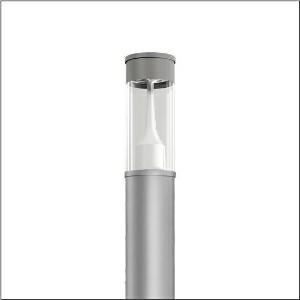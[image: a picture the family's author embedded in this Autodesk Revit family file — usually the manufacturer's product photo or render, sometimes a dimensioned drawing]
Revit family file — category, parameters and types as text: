
# Revit family: city-light_260_iq___pl1_2s_5xa5295of14h_8957
name_source: partatom
category: Lighting Fixtures
units: mm (PartAtom-declared; Revit-internal decimal feet)

## family parameters
Cut with Voids When Loaded = No
Host = Face
Light Source = No
Part Type = Normal
Room Calculation Point = No
Round Connector Dimension = Use Diameter
Shared = No

## types (1)
- --- (1 x LED, 2970 lm, 21.8 W, 2700K)
    Apparent Load = 22 VA
    CIE Flux Codes = 23 62 94 96 100
    Color Rendering = 70
    Color Temperature = 2700K
    Default Elevation = 1800 mm
    Description = City-Light 260 iQ, light pillar, Module 540 iQ-SR, primary light control with 3 zone facetted reflector, of plastic, silver coated, highly specular, structured, primary optical cover: cover, of PMMA, transparent, partly coated, light distribution: PL1.2s, primary light characteristic: symmetric, LED, High Power LED, rated luminous flux: 2.970lm, luminous efficacy: 136lm/W, light colour: 727, colour temperature: 2700K, control gear: iQ Street-Remote, control: pre-setting: logarithmic dimming characteristic, Street-Remote, Auto-Match, Temp-Guard, Lumen-Switch, Night-Set, Smart-Wire, Light-Fading, Desk-Remote (wireless, voltage-free reading and setting of iQ features in the workshop via application-optimized NFC function/RFID function), optimised constant luminous flux control (CLO 2.0), with terminal, 6-pole, max. 2.5mm², mains connection: 230..240V, AC, 50/60Hz, start of lifetime: 22W, end of service life: 23W, reduction: 11W, luminaire housing, cylindrical, of extruded aluminium section, coated, Siteco® metallic grey (DB 702S), length: 2.600mm, diameter: 200mm, Module 540 iQ-SR, traffic white (RAL 9016), equipment: standard, protection rating (complete): IP65, insulation class (complete): insulation class II (safety insulation), certification: CE, ENEC, VDE, packaging unit: 1 piece

Light Distribution: PL1.2s
    Height = 500 mm
    Lamp = 1 x LED
    Lamp Light Flux = 2970 lm
    Lamp Power = 21.8 W
    Lamp count = 1
    Length = 200 mm  [stored 0.656168 ft]
    Luminous efficacy = 136 lm/W
    Manufacturer = Siteco
    ModVariant = No
    Model = 5XA5295OF14H
    Mounting Place = Floor
    Mounting Type = Freestanding
    Number of Poles = 1
    OnlyDefault = Yes
    Power Factor = 1
    Product Name = City-Light 260 iQ | PL1.2s
    Product group = light pillar
    ProductGroupID = 1301
    Protection Class = Protection class II
    Protection Degree = IP 65
    RLX_Detail_Level = 1
    RLX_Emergency_Light_Flux = 0 lm
    RLX_Emergency_Type = 0
    RLX_Emergency_Type_DB = No
    RlxData = <blob elided: 21841 chars, md5=e8835069>
    Socket = socket
    Standby Power = 0 W
    System Light Flux = 2970 lm
    System Power = 22 W
    Type Comments = factory setting: luminous flux: 100 % | dim-lin: 254 | 456 mA
    Type Image = l_1006920.jpg
    URL = http://relux.com
    VarID = @adj_166417
    Voltage = 0 V
    Weight = 0.00 kg
    Width = 0 mm  [stored 0 ft]

note: [stored X ft] marks values corroborated as IEEE doubles in the binary element streams (Revit-internal decimal feet)

## geometry (parser evidence)
native form markers: Blend x4, Sweep x10
no freeform markers — native parametric forms only
